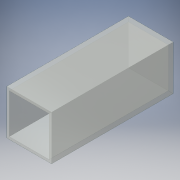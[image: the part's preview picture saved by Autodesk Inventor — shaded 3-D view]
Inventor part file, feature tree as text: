
AUTODESK INVENTOR PART (.ipt)
format: ipt  version: 2016 (Build 200138000, 138)  size: 104,448 bytes
history: native  units: mm
features: extrude x2, sketch x2
ambient origin geometry x8: Origin, YZ Plane, XZ Plane, XY Plane, X Axis, Y Axis, Z Axis, Center Point
bodies: Solid1 (feature_tree)
feature tree (4):
  extrude  "Extrusion1"  Depth=45.0mm
  extrude  "Extrusion2"  Depth=40.0mm
  sketch  "Sketch1"  dims[d0=45.0mm d1=45.0mm]
  sketch  "Sketch2"  dims[d2=40.0mm d3=40.0mm d4=120.0mm d5=0.0mm d6=2.5mm d7=0.0mm]
